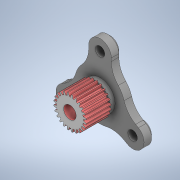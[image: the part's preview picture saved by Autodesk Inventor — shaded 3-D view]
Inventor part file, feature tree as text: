
AUTODESK INVENTOR PART (.ipt)
format: ipt  version: 2022 (Build 260153000, 153)  size: 445,440 bytes
history: mixed  units: mm
features: other x3, extrude x1, sketch x1, imported_body x1
ambient origin geometry x8: Origin, YZ Plane, XZ Plane, XY Plane, X Axis, Y Axis, Z Axis, Center Point
bodies: Solid1 (imported_parasolid)
feature tree (6):
  other  "Planet_Carrier_Modifed_with_sun_gear.iam"
  other  "Plamet_Carrier.ipt:1"
  other  "24_Teeth_Sun_Gear.ipt:1"
  extrude  "Extrusion1"  Depth=5.0mm TaperAngle=0.0deg
  sketch  "Sketch1"  dims[d0=10.0mm d1=5.0mm d2=0.0mm]
  imported_body  NMx_Import_Brep_tag  [imported B-rep: ~177 faces, bbox_mm=[31.788121, 26.496463, 16.0]]
